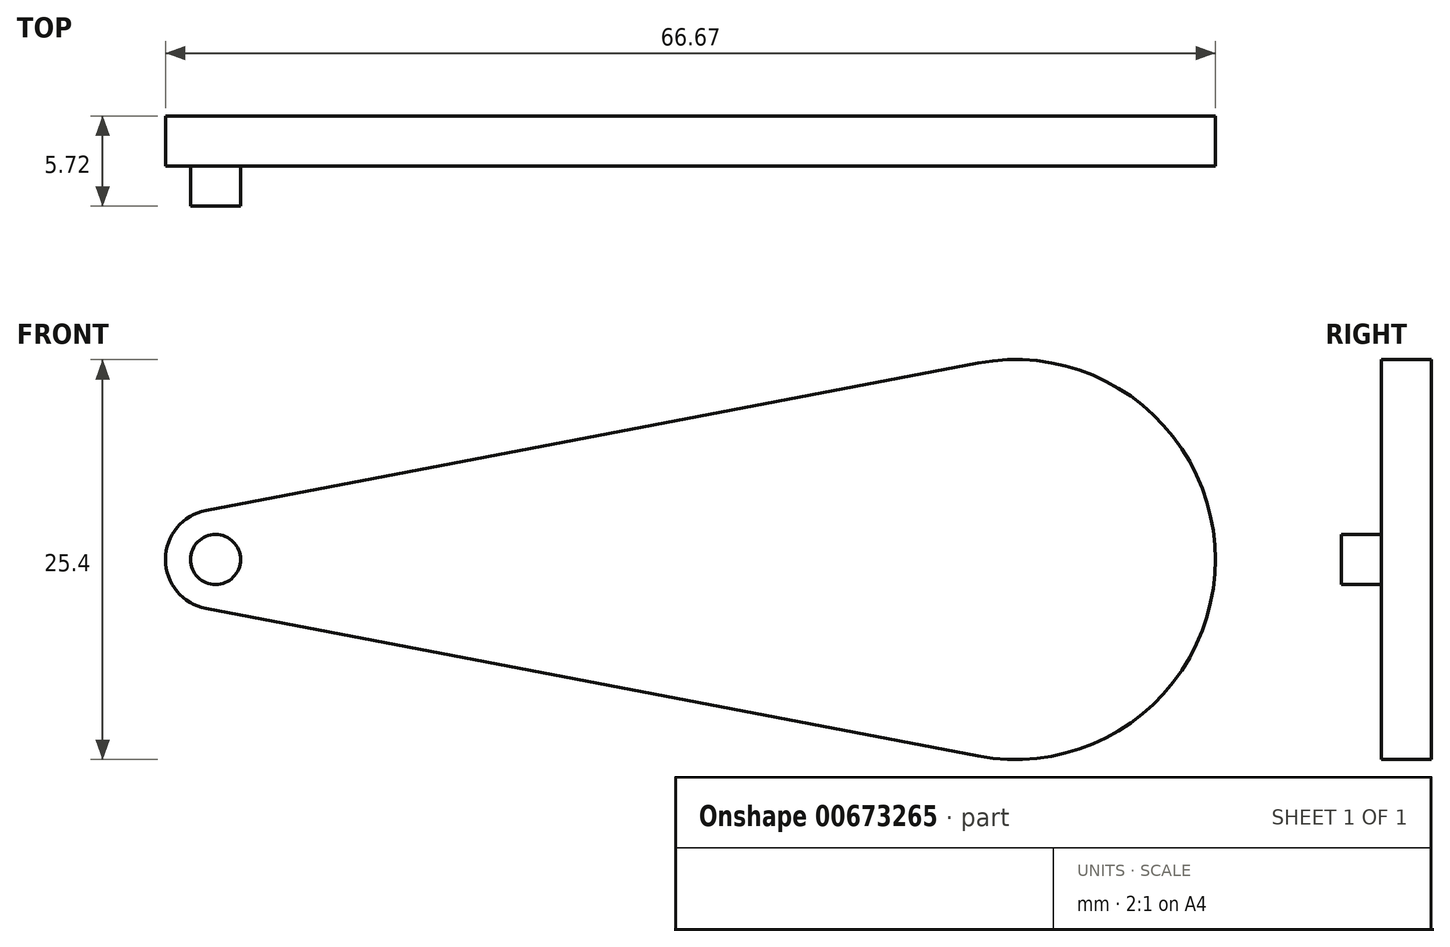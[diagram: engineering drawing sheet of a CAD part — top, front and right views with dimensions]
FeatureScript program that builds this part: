
annotation { "Feature Type Name" : "Feature", "Feature Type Description" : "" }
export const myFeature = defineFeature(function(context is Context, id is Id, definition is map)
    precondition{}
    {
        {
            var Q0;
            Q0=qCreatedBy(makeId("Front.planeOp"),FACE);
            var sketch = newSketch(context, id + "F0", { "sketchPlane" : qUnion([Q0])});
            skCircle(sketch, "E0", {"center": v(0, 0) * mm, "radius": 1.59 * mm});
            skArc(sketch, "E1", {"start": v(-0.6, 3.12) * mm, "mid": v(-3.18, 0) * mm, "end": v(-0.6, -3.12) * mm});
            skArc(sketch, "E2", {"start": v(48.42, -12.47) * mm, "mid": v(63.5, 0) * mm, "end": v(48.42, 12.47) * mm});
            skLineSegment(sketch, "E3", {"start": v(-0.6, 3.12) * mm, "end": v(48.42, 12.47) * mm});
            skLineSegment(sketch, "E4", {"start": v(-0.6, -3.12) * mm, "end": v(48.42, -12.47) * mm});
            skSolve(sketch);
        }
        {
            var Q0;
            Q0=makeQuery(id+"F0.imprint","IMPRINT",FACE,{"disambiguationData":[TD([[makeQuery(id+"F0.imprint","IMPRINT",EDGE,{"derivedFrom":sQuery(id+"F0.wireOp",EDGE,"E0")}),1.0]])]});
            extrude(context, id + "F1", {"entities" : qUnion([Q0]), "depth" : 5.7 * mm});
        }
        {
            var Q0;
            Q0=qSketchRegion(id+"F0",true);
            extrude(context, id + "F2", {"entities" : qUnion([Q0]), "operationType" : NewBodyOperationType.ADD, "depth" : 3.17 * mm});
        }
    });
